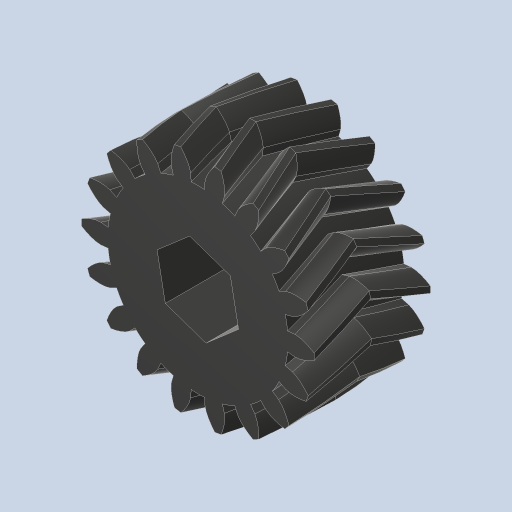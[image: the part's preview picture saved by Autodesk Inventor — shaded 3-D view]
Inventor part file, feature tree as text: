
AUTODESK INVENTOR PART (.ipt)
format: ipt  version: 2023.4 (Build 274418000, 418)  size: 716,288 bytes
history: native  units: in
note: dims shown in document units (in); Inventor stores cm internally (conversion verified against a paired STEP export)
features: other x2, extrude x1, sketch x1
ambient origin geometry x8: Origin, YZ Plane, XZ Plane, XY Plane, X Axis, Y Axis, Z Axis, Center Point
bodies: Solid1 (feature_tree)
feature tree (4):
  extrude  "Extrusion1"  TaperAngle=0.0deg  [1 undecoded]
  other  "DIAMETRIC PITCH"
  sketch  "Sketch1"  dims[d0=0.505in d1=0.0in d2=0.0in d3=1.4173in]
  other  "Helical 2M 18T"
note: 1 required parameter value undecoded (feature->parameter linkage not recoverable at this tier; creation-order binding heuristic only, values carry confidence <= 0.55)
